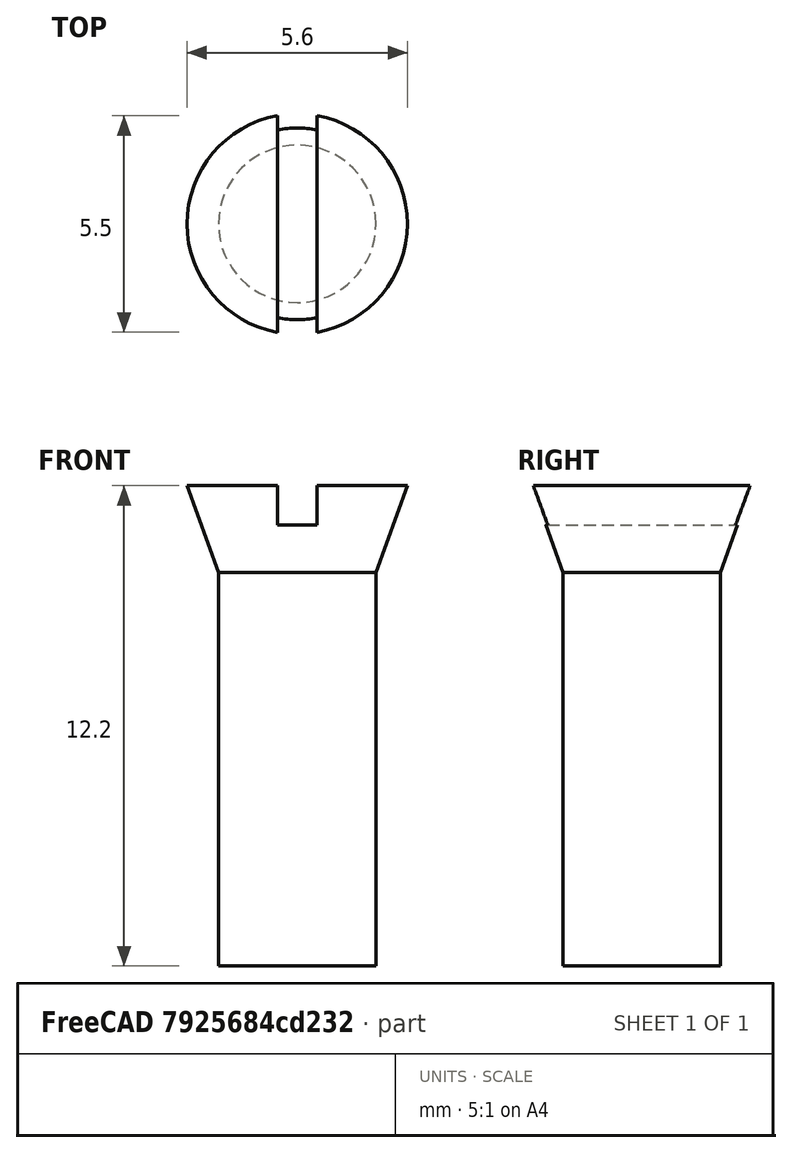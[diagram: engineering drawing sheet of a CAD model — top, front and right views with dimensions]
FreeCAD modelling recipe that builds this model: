
FCSTD DOCUMENT  (FreeCAD 0.21R33771 (Git))
Label: OJT1_T14R01_cargol
License: All rights reserved
LicenseURL: http://en.wikipedia.org/wiki/All_rights_reserved
objects: Part::Cylinder×1, Part::Cone×1, Part::Box×1, Part::Cut×1, Part::MultiFuse×1
note: 5 computed .brp shape members not serialized (recipe doc carries the construction recipe); baked Part::Feature solids carry a one-line shape summary decoded from their .brp

FEATURE [Part::Cylinder] Cylinder
  Angle = 360
  AttacherType = Attacher::AttachEngine3D
  FirstAngle = 0
  Height = 10
  Radius = 2
  SecondAngle = 0
FEATURE [Part::Cone] Cone
  Angle = 360
  AttacherType = Attacher::AttachEngine3D
  Height = 2.2
  Placement = pos=(0,0,10) rot=(0,0,1;0rad)
  Radius1 = 2
  Radius2 = 2.8
FEATURE [Part::Box] Box  label="Cube"
  AttacherType = Attacher::AttachEngine3D
  Height = 1
  Length = 1
  Placement = pos=(-0.5,-4,11.2) rot=(0,0,1;0rad)
  Width = 10
FEATURE [Part::Cut] Cut
  Base = -> Cone
  Refine = true
  Tool = -> Box
FEATURE [Part::MultiFuse] Fusion  label="cargol"
  Refine = true
  Shapes = -> [Cylinder,Cut]
